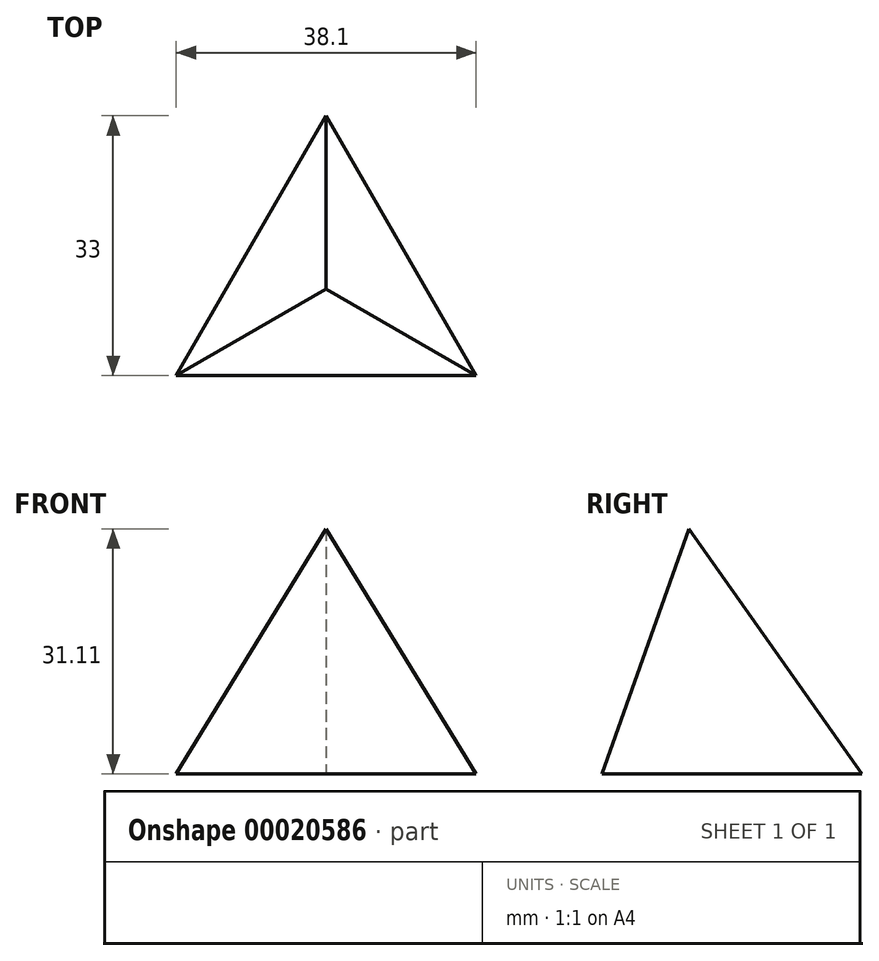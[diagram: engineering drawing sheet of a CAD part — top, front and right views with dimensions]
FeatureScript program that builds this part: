
annotation { "Feature Type Name" : "Feature", "Feature Type Description" : "" }
export const myFeature = defineFeature(function(context is Context, id is Id, definition is map)
    precondition{}
    {
        {
            var Q0;
            Q0=qCreatedBy(makeId("Top.planeOp"),FACE);
            var sketch = newSketch(context, id + "F0", { "sketchPlane" : qUnion([Q0])});
            skLineSegment(sketch, "E0", {"start": v(0, 0) * mm, "end": v(38.1, 0) * mm});
            skLineSegment(sketch, "E1", {"start": v(38.1, 0) * mm, "end": v(19.05, 33) * mm});
            skLineSegment(sketch, "E2", {"start": v(19.05, 33) * mm, "end": v(0, 0) * mm});
            skSolve(sketch);
        }
        {
            var Q0;
            Q0=makeQuery(id+"F0.imprint","IMPRINT",FACE,{"disambiguationData":[TD([[makeQuery(id+"F0.imprint","IMPRINT",EDGE,{"derivedFrom":sQuery(id+"F0.wireOp",EDGE,"E0")}),1.0]])]});
            extrude(context, id + "F1", {"entities" : qUnion([Q0]), "depth" : 31.1 * mm, "hasDraft" : true, "draftAngle" : 19.47 * degree, "draftPullDirection" : true});
        }
    });
